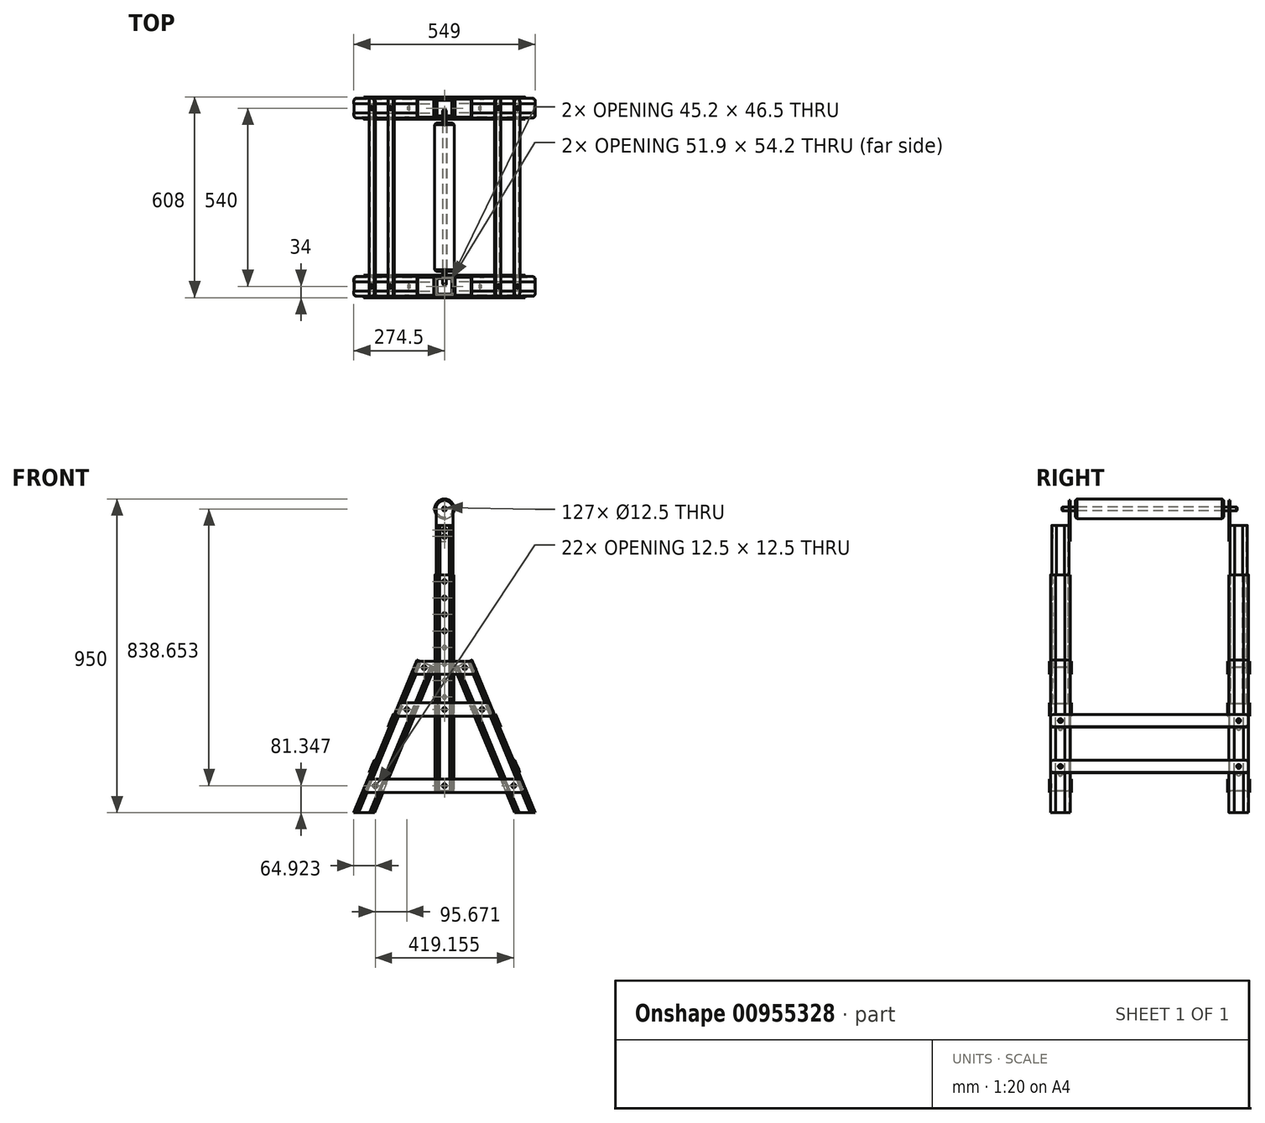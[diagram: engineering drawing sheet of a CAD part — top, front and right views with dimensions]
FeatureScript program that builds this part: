
annotation { "Feature Type Name" : "Feature", "Feature Type Description" : "" }
export const myFeature = defineFeature(function(context is Context, id is Id, definition is map)
    precondition{}
    {
        {
            var Q0;
            Q0=qCreatedBy(makeId("Front.planeOp"),FACE);
            var sketch = newSketch(context, id + "F0", { "sketchPlane" : qUnion([Q0])});
            skLineSegment(sketch, "E0", {"start": v(0, 0) * mm, "end": v(-62.45, 0) * mm});
            skLineSegment(sketch, "E1", {"start": v(-62.45, 0) * mm, "end": v(-244.65, 439.86) * mm});
            skLineSegment(sketch, "E2", {"start": v(-244.65, 439.86) * mm, "end": v(-191.34, 461.94) * mm});
            skLineSegment(sketch, "E3", {"start": v(-191.34, 461.94) * mm, "end": v(0, 0) * mm});
            skLineSegment(sketch, "E4", {"start": v(-218, 450.9) * mm, "end": v(-31.23, 0) * mm, "construction": true});
            skCircle(sketch, "E5", {"center": v(-213.02, 438.89) * mm, "radius": 6.25 * mm});
            skCircle(sketch, "E6", {"center": v(-64.92, 81.35) * mm, "radius": 6.25 * mm});
            skCircle(sketch, "E7", {"center": v(-160.6, 312.32) * mm, "radius": 6.25 * mm});
            skSolve(sketch);
        }
        {
            var Q0;
            Q0 = qSketchRegion(id + "F0", true);
            extrude(context, id + "F1", {"entities" : qUnion([Q0]), "depth" : 60 * mm, "offsetDistance" : 25 * mm});
        }
        {
            var Q0;
            Q0=makeQuery(id+"F1.opExtrude","SWEPT_FACE",FACE,{"disambiguationData":[OSD([sQuery(id+"F0.wireOp",EDGE,"E3")])]});
            var sketch = newSketch(context, id + "F2", { "sketchPlane" : qUnion([Q0])});
            skLineSegment(sketch, "E8", {"start": v(-30, 500) * mm, "end": v(-30, 0) * mm, "construction": true});
            skCircle(sketch, "E9", {"center": v(-30, 150) * mm, "radius": 6.25 * mm});
            skCircle(sketch, "E10", {"center": v(-30, 300) * mm, "radius": 6.25 * mm});
            skSolve(sketch);
        }
        {
            var Q0;
            Q0 = qSketchRegion(id + "F2", true);
            var Q1;
            Q1=makeQuery(id+"F1.opExtrude","SWEPT_FACE",FACE,{"disambiguationData":[OSD([sQuery(id+"F0.wireOp",EDGE,"E1")])]});
            extrude(context, id + "F3", {"entities" : qUnion([Q0]), "operationType" : NewBodyOperationType.REMOVE, "endBound" : BoundingType.UP_TO_SURFACE, "oppositeDirection" : true, "depth" : 25 * mm, "endBoundEntityFace" : qUnion([Q1]), "offsetDistance" : 25 * mm});
        }
        {
            var Q0;
            Q0=makeQuery(id+"F1.opExtrude","CAP_EDGE",EDGE,{"disambiguationData":[OSD([sQuery(id+"F0.wireOp",EDGE,"E1")])],"isStart":false});
            var Q1;
            Q1=makeQuery(id+"F1.opExtrude","CAP_EDGE",EDGE,{"disambiguationData":[OSD([sQuery(id+"F0.wireOp",EDGE,"E3")])],"isStart":false});
            var Q2;
            Q2=makeQuery(id+"F1.opExtrude","CAP_EDGE",EDGE,{"disambiguationData":[OSD([sQuery(id+"F0.wireOp",EDGE,"E1")])],"isStart":true});
            var Q3;
            Q3=makeQuery(id+"F1.opExtrude","CAP_EDGE",EDGE,{"disambiguationData":[OSD([sQuery(id+"F0.wireOp",EDGE,"E3")])],"isStart":true});
            fillet(context, id + "F4", {"entities" : qUnion([Q0, Q1, Q2, Q3]), "radius" : 7.5 * mm, "tangentPropagation" : true, "allowEdgeOverflow" : false});
        }
        {
            var Q0;
            Q0=makeQuery(id+"F1.opExtrude","SWEPT_FACE",FACE,{"disambiguationData":[OSD([sQuery(id+"F0.wireOp",EDGE,"E2")])]});
            var sketch = newSketch(context, id + "F5", { "sketchPlane" : qUnion([Q0])});
            skLineSegment(sketch, "E11", {"start": v(-57.7, -30) * mm, "end": v(-28.85, -30) * mm, "construction": true});
            skLineSegment(sketch, "E12", {"start": v(-28.85, -30) * mm, "end": v(-28.85, -60) * mm, "construction": true});
            skArc(sketch, "E13.0", {"start": v(-54.8, -52.5) * mm, "mid": v(-53.45, -55.75) * mm, "end": v(-50.2, -57.1) * mm});
            skLineSegment(sketch, "E14", {"start": v(-57.4, -30) * mm, "end": v(-57.4, -44) * mm});
            skLineSegment(sketch, "E15", {"start": v(-57.4, -44) * mm, "end": v(-57.7, -44) * mm});
            skLineSegment(sketch, "E16", {"start": v(-50.2, -60) * mm, "end": v(-49.2, -59) * mm});
            skLineSegment(sketch, "E17", {"start": v(-49.2, -59) * mm, "end": v(-48.2, -60) * mm});
            skLineSegment(sketch, "E18", {"start": v(-48.2, -60) * mm, "end": v(-47.2, -59) * mm});
            skLineSegment(sketch, "E19", {"start": v(-47.2, -59) * mm, "end": v(-46.2, -60) * mm});
            skLineSegment(sketch, "E20", {"start": v(-46.2, -60) * mm, "end": v(-45.2, -59) * mm});
            skLineSegment(sketch, "E21", {"start": v(-45.2, -59) * mm, "end": v(-44.2, -60) * mm});
            skLineSegment(sketch, "E22", {"start": v(-50.2, -57.1) * mm, "end": v(-28.85, -57.1) * mm});
            skLineSegment(sketch, "E23", {"start": v(-54.8, -52.5) * mm, "end": v(-54.8, -30) * mm});
            skLineSegment(sketch, "E24.MirrorCS", {"start": v(-0.3, -44) * mm, "end": v(0, -44) * mm});
            skLineSegment(sketch, "E25.MirrorCS", {"start": v(-12.5, -59) * mm, "end": v(-13.5, -60) * mm});
            skLineSegment(sketch, "E26.MirrorCS", {"start": v(-7.5, -60) * mm, "end": v(-8.5, -59) * mm});
            skLineSegment(sketch, "E27.MirrorCS", {"start": v(-8.5, -59) * mm, "end": v(-9.5, -60) * mm});
            skLineSegment(sketch, "E28.MirrorCS", {"start": v(-11.5, -60) * mm, "end": v(-12.5, -59) * mm});
            skLineSegment(sketch, "E29.MirrorCS", {"start": v(-10.5, -59) * mm, "end": v(-11.5, -60) * mm});
            skLineSegment(sketch, "E30.MirrorCS", {"start": v(-9.5, -60) * mm, "end": v(-10.5, -59) * mm});
            skLineSegment(sketch, "E31.MirrorCS", {"start": v(-0.3, -30) * mm, "end": v(-0.3, -44) * mm});
            skLineSegment(sketch, "E32.MirrorCS", {"start": v(-7.5, -57.1) * mm, "end": v(-28.85, -57.1) * mm});
            skLineSegment(sketch, "E33.MirrorCS", {"start": v(-2.9, -52.5) * mm, "end": v(-2.9, -30) * mm});
            skArc(sketch, "E34.MirrorCS", {"start": v(-2.9, -52.5) * mm, "mid": v(-4.25, -55.75) * mm, "end": v(-7.5, -57.1) * mm});
            skLineSegment(sketch, "E35.MirrorCS", {"start": v(-57.4, -16) * mm, "end": v(-57.7, -16) * mm});
            skLineSegment(sketch, "E36.MirrorCS", {"start": v(-50.2, 0) * mm, "end": v(-49.2, -1) * mm});
            skLineSegment(sketch, "E37.MirrorCS", {"start": v(-45.2, -1) * mm, "end": v(-44.2, 0) * mm});
            skLineSegment(sketch, "E38.MirrorCS", {"start": v(-47.2, -1) * mm, "end": v(-46.2, 0) * mm});
            skLineSegment(sketch, "E39.MirrorCS", {"start": v(-48.2, 0) * mm, "end": v(-47.2, -1) * mm});
            skLineSegment(sketch, "E40.MirrorCS", {"start": v(-49.2, -1) * mm, "end": v(-48.2, 0) * mm});
            skLineSegment(sketch, "E41.MirrorCS", {"start": v(-46.2, 0) * mm, "end": v(-45.2, -1) * mm});
            skLineSegment(sketch, "E42.MirrorCS", {"start": v(-57.4, -30) * mm, "end": v(-57.4, -16) * mm});
            skArc(sketch, "E43.MirrorCS", {"start": v(-54.8, -7.5) * mm, "mid": v(-53.45, -4.25) * mm, "end": v(-50.2, -2.9) * mm});
            skLineSegment(sketch, "E44.MirrorCS", {"start": v(-50.2, -2.9) * mm, "end": v(-28.85, -2.9) * mm});
            skLineSegment(sketch, "E45.MirrorCS", {"start": v(-54.8, -7.5) * mm, "end": v(-54.8, -30) * mm});
            skLineSegment(sketch, "E46.MirrorCS", {"start": v(-0.3, -16) * mm, "end": v(0, -16) * mm});
            skLineSegment(sketch, "E47.MirrorCS", {"start": v(-8.5, -1) * mm, "end": v(-9.5, 0) * mm});
            skLineSegment(sketch, "E48.MirrorCS", {"start": v(-11.5, 0) * mm, "end": v(-12.5, -1) * mm});
            skLineSegment(sketch, "E49.MirrorCS", {"start": v(-10.5, -1) * mm, "end": v(-11.5, 0) * mm});
            skLineSegment(sketch, "E50.MirrorCS", {"start": v(-9.5, 0) * mm, "end": v(-10.5, -1) * mm});
            skLineSegment(sketch, "E51.MirrorCS", {"start": v(-12.5, -1) * mm, "end": v(-13.5, 0) * mm});
            skLineSegment(sketch, "E52.MirrorCS", {"start": v(-7.5, 0) * mm, "end": v(-8.5, -1) * mm});
            skLineSegment(sketch, "E53.MirrorCS", {"start": v(-0.3, -30) * mm, "end": v(-0.3, -16) * mm});
            skLineSegment(sketch, "E54.MirrorCS", {"start": v(-2.9, -7.5) * mm, "end": v(-2.9, -30) * mm});
            skArc(sketch, "E55.MirrorCS", {"start": v(-2.9, -7.5) * mm, "mid": v(-4.25, -4.25) * mm, "end": v(-7.5, -2.9) * mm});
            skLineSegment(sketch, "E56.MirrorCS", {"start": v(-7.5, -2.9) * mm, "end": v(-28.85, -2.9) * mm});
            skSolve(sketch);
        }
        {
            var Q0;
            {var subQ0=sQuery(id+"F5.wireOp",EDGE,"E20");Q0=makeQuery(id+"F5.imprint","IMPRINT",FACE,{"disambiguationData":[TD([[makeQuery(id+"F5.imprint","IMPRINT",EDGE,{"derivedFrom":subQ0}),-1.0]])]});}
            var Q1;
            {var subQ0=sQuery(id+"F5.wireOp",EDGE,"E18");Q1=makeQuery(id+"F5.imprint","IMPRINT",FACE,{"disambiguationData":[TD([[makeQuery(id+"F5.imprint","IMPRINT",EDGE,{"derivedFrom":subQ0}),-1.0]])]});}
            var Q2;
            {var subQ0=sQuery(id+"F5.wireOp",EDGE,"E16");Q2=makeQuery(id+"F5.imprint","IMPRINT",FACE,{"disambiguationData":[TD([[makeQuery(id+"F5.imprint","IMPRINT",EDGE,{"derivedFrom":subQ0}),-1.0]])]});}
            var Q3;
            {var subQ0=sQuery(id+"F5.wireOp",EDGE,"E26.MirrorCS");Q3=makeQuery(id+"F5.imprint","IMPRINT",FACE,{"disambiguationData":[TD([[makeQuery(id+"F5.imprint","IMPRINT",EDGE,{"derivedFrom":subQ0}),1.0]])]});}
            var Q4;
            {var subQ0=sQuery(id+"F5.wireOp",EDGE,"E29.MirrorCS");Q4=makeQuery(id+"F5.imprint","IMPRINT",FACE,{"disambiguationData":[TD([[makeQuery(id+"F5.imprint","IMPRINT",EDGE,{"derivedFrom":subQ0}),1.0]])]});}
            var Q5;
            {var subQ0=sQuery(id+"F5.wireOp",EDGE,"E25.MirrorCS");Q5=makeQuery(id+"F5.imprint","IMPRINT",FACE,{"disambiguationData":[TD([[makeQuery(id+"F5.imprint","IMPRINT",EDGE,{"derivedFrom":subQ0}),1.0]])]});}
            var Q6;
            {var subQ1=sQuery(id+"F5.wireOp",EDGE,"E24.MirrorCS");Q6=makeQuery(id+"F5.imprint","IMPRINT",FACE,{"disambiguationData":[TD([[makeQuery(id+"F5.imprint","IMPRINT",EDGE,{"derivedFrom":subQ1}),1.0]])]});}
            var Q7;
            Q7=makeQuery(id+"F5.imprint","IMPRINT",FACE,{"disambiguationData":[TD([[makeQuery(id+"F5.imprint","IMPRINT",EDGE,{"derivedFrom":sQuery(id+"F5.wireOp",EDGE,"E14")}),-1.0]])]});
            var Q8;
            {var subQ0=sQuery(id+"F5.wireOp",EDGE,"E36.MirrorCS");Q8=makeQuery(id+"F5.imprint","IMPRINT",FACE,{"disambiguationData":[TD([[makeQuery(id+"F5.imprint","IMPRINT",EDGE,{"derivedFrom":subQ0}),1.0]])]});}
            var Q9;
            {var subQ0=sQuery(id+"F5.wireOp",EDGE,"E38.MirrorCS");Q9=makeQuery(id+"F5.imprint","IMPRINT",FACE,{"disambiguationData":[TD([[makeQuery(id+"F5.imprint","IMPRINT",EDGE,{"derivedFrom":subQ0}),1.0]])]});}
            var Q10;
            {var subQ0=sQuery(id+"F5.wireOp",EDGE,"E37.MirrorCS");Q10=makeQuery(id+"F5.imprint","IMPRINT",FACE,{"disambiguationData":[TD([[makeQuery(id+"F5.imprint","IMPRINT",EDGE,{"derivedFrom":subQ0}),1.0]])]});}
            var Q11;
            {var subQ0=sQuery(id+"F5.wireOp",EDGE,"E47.MirrorCS");Q11=makeQuery(id+"F5.imprint","IMPRINT",FACE,{"disambiguationData":[TD([[makeQuery(id+"F5.imprint","IMPRINT",EDGE,{"derivedFrom":subQ0}),-1.0]])]});}
            var Q12;
            {var subQ0=sQuery(id+"F5.wireOp",EDGE,"E49.MirrorCS");Q12=makeQuery(id+"F5.imprint","IMPRINT",FACE,{"disambiguationData":[TD([[makeQuery(id+"F5.imprint","IMPRINT",EDGE,{"derivedFrom":subQ0}),-1.0]])]});}
            var Q13;
            {var subQ0=sQuery(id+"F5.wireOp",EDGE,"E48.MirrorCS");Q13=makeQuery(id+"F5.imprint","IMPRINT",FACE,{"disambiguationData":[TD([[makeQuery(id+"F5.imprint","IMPRINT",EDGE,{"derivedFrom":subQ0}),-1.0]])]});}
            var Q14;
            Q14=makeQuery(id+"F5.imprint","IMPRINT",FACE,{"disambiguationData":[TD([[makeQuery(id+"F5.imprint","IMPRINT",EDGE,{"derivedFrom":sQuery(id+"F5.wireOp",EDGE,"E13.0")}),1.0]])]});
            var Q15;
            Q15=makeQuery(id+"F1.opExtrude","SWEPT_FACE",FACE,{"disambiguationData":[OSD([sQuery(id+"F0.wireOp",EDGE,"E0")])]});
            extrude(context, id + "F6", {"entities" : qUnion([Q0, Q1, Q2, Q3, Q4, Q5, Q6, Q7, Q8, Q9, Q10, Q11, Q12, Q13, Q14]), "operationType" : NewBodyOperationType.REMOVE, "endBound" : BoundingType.UP_TO_SURFACE, "oppositeDirection" : true, "depth" : 25 * mm, "endBoundEntityFace" : qUnion([Q15]), "offsetDistance" : 25 * mm});
        }
        {
            var Q0;
            Q0=makeQuery(id+"F1.opExtrude","CAP_FACE",FACE,{"disambiguationData":[OSD([sQuery(id+"F0.wireOp",EDGE,"E0"),sQuery(id+"F0.wireOp",EDGE,"E1"),sQuery(id+"F0.wireOp",EDGE,"E2"),sQuery(id+"F0.wireOp",EDGE,"E3"),sQuery(id+"F0.wireOp",EDGE,"E5"),sQuery(id+"F0.wireOp",EDGE,"E6")])],"isStart":false});
            var sketch = newSketch(context, id + "F7", { "sketchPlane" : qUnion([Q0])});
            skLineSegment(sketch, "E57", {"start": v(-245.65, 720) * mm, "end": v(-245.65, 66.35) * mm});
            skLineSegment(sketch, "E58", {"start": v(-245.65, 66.35) * mm, "end": v(-303.35, 66.35) * mm});
            skLineSegment(sketch, "E59", {"start": v(-303.35, 66.35) * mm, "end": v(-303.35, 720) * mm});
            skLineSegment(sketch, "E60", {"start": v(-303.35, 720) * mm, "end": v(-245.65, 720) * mm});
            skLineSegment(sketch, "E61", {"start": v(-303.35, 75.1) * mm, "end": v(24.53, 75.1) * mm, "construction": true});
            skLineSegment(sketch, "E62", {"start": v(-274.5, 720) * mm, "end": v(-274.5, 66.35) * mm, "construction": true});
            skCircle(sketch, "E63", {"center": v(-274.5, 81.35) * mm, "radius": 6.25 * mm});
            skLineSegment(sketch, "E64", {"start": v(-303.35, 306.07) * mm, "end": v(155.56, 306.07) * mm, "construction": true});
            skCircle(sketch, "E65", {"center": v(-274.5, 312.32) * mm, "radius": 6.25 * mm});
            skCircle(sketch, "E66", {"center": v(-274.5, 650) * mm, "radius": 6.25 * mm});
            skCircle(sketch, "E67", {"center": v(-274.5, 600) * mm, "radius": 6.25 * mm});
            skCircle(sketch, "E68", {"center": v(-274.5, 700) * mm, "radius": 6.25 * mm});
            skCircle(sketch, "E69", {"center": v(-274.5, 550) * mm, "radius": 6.25 * mm});
            skSolve(sketch);
        }
        {
            var Q0;
            Q0 = qSketchRegion(id + "F7", true);
            extrude(context, id + "F8", {"entities" : qUnion([Q0]), "oppositeDirection" : true, "depth" : 60 * mm, "offsetDistance" : 25 * mm});
        }
        {
            var Q0;
            Q0=makeQuery(id+"F8.opExtrude","CAP_EDGE",EDGE,{"disambiguationData":[OSD([sQuery(id+"F7.wireOp",EDGE,"E59")])],"isStart":false});
            var Q1;
            Q1=makeQuery(id+"F8.opExtrude","CAP_EDGE",EDGE,{"disambiguationData":[OSD([sQuery(id+"F7.wireOp",EDGE,"E59")])],"isStart":true});
            var Q2;
            Q2=makeQuery(id+"F8.opExtrude","CAP_EDGE",EDGE,{"disambiguationData":[OSD([sQuery(id+"F7.wireOp",EDGE,"E57")])],"isStart":true});
            var Q3;
            Q3=makeQuery(id+"F8.opExtrude","CAP_EDGE",EDGE,{"disambiguationData":[OSD([sQuery(id+"F7.wireOp",EDGE,"E57")])],"isStart":false});
            fillet(context, id + "F9", {"entities" : qUnion([Q0, Q1, Q2, Q3]), "radius" : 7.5 * mm, "tangentPropagation" : true, "allowEdgeOverflow" : false});
        }
        {
            var Q0;
            Q0=makeQuery(id+"F8.opExtrude","SWEPT_FACE",FACE,{"disambiguationData":[OSD([sQuery(id+"F7.wireOp",EDGE,"E60")])]});
            var sketch = newSketch(context, id + "F10", { "sketchPlane" : qUnion([Q0])});
            skLineSegment(sketch, "E70", {"start": v(-274.5, -60) * mm, "end": v(-274.5, -30) * mm, "construction": true});
            skPoint(sketch, "E70.endSnap0", {"position": v(-303.35, -30) * mm});
            skLineSegment(sketch, "E71", {"start": v(-274.5, -30) * mm, "end": v(-303.35, -30) * mm, "construction": true});
            skLineSegment(sketch, "E72", {"start": v(-295.85, -60) * mm, "end": v(-294.85, -59) * mm});
            skLineSegment(sketch, "E73", {"start": v(-294.85, -59) * mm, "end": v(-293.85, -60) * mm});
            skLineSegment(sketch, "E74", {"start": v(-293.85, -60) * mm, "end": v(-292.85, -59) * mm});
            skLineSegment(sketch, "E75", {"start": v(-292.85, -59) * mm, "end": v(-291.85, -60) * mm});
            skLineSegment(sketch, "E76", {"start": v(-291.85, -60) * mm, "end": v(-290.85, -59) * mm});
            skLineSegment(sketch, "E77", {"start": v(-290.85, -59) * mm, "end": v(-289.85, -60) * mm});
            skLineSegment(sketch, "E78", {"start": v(-303.05, -30) * mm, "end": v(-303.05, -44) * mm});
            skLineSegment(sketch, "E79", {"start": v(-303.05, -44) * mm, "end": v(-303.35, -44) * mm});
            skArc(sketch, "E80.0", {"start": v(-300.45, -52.5) * mm, "mid": v(-299.1, -55.75) * mm, "end": v(-295.85, -57.1) * mm});
            skLineSegment(sketch, "E81", {"start": v(-295.85, -57.1) * mm, "end": v(-274.5, -57.1) * mm});
            skLineSegment(sketch, "E82", {"start": v(-300.45, -52.5) * mm, "end": v(-300.45, -30) * mm});
            skLineSegment(sketch, "E83.MirrorCS", {"start": v(-255.15, -60) * mm, "end": v(-256.15, -59) * mm});
            skLineSegment(sketch, "E84.MirrorCS", {"start": v(-245.95, -44) * mm, "end": v(-245.65, -44) * mm});
            skLineSegment(sketch, "E85.MirrorCS", {"start": v(-254.15, -59) * mm, "end": v(-255.15, -60) * mm});
            skLineSegment(sketch, "E86.MirrorCS", {"start": v(-256.15, -59) * mm, "end": v(-257.15, -60) * mm});
            skLineSegment(sketch, "E87.MirrorCS", {"start": v(-257.15, -60) * mm, "end": v(-258.15, -59) * mm});
            skLineSegment(sketch, "E88.MirrorCS", {"start": v(-253.15, -60) * mm, "end": v(-254.15, -59) * mm});
            skLineSegment(sketch, "E89.MirrorCS", {"start": v(-258.15, -59) * mm, "end": v(-259.15, -60) * mm});
            skLineSegment(sketch, "E90.MirrorCS", {"start": v(-248.55, -52.5) * mm, "end": v(-248.55, -30) * mm});
            skLineSegment(sketch, "E91.MirrorCS", {"start": v(-245.95, -30) * mm, "end": v(-245.95, -44) * mm});
            skLineSegment(sketch, "E92.MirrorCS", {"start": v(-253.15, -57.1) * mm, "end": v(-274.5, -57.1) * mm});
            skArc(sketch, "E93.MirrorCS", {"start": v(-248.55, -52.5) * mm, "mid": v(-249.9, -55.75) * mm, "end": v(-253.15, -57.1) * mm});
            skLineSegment(sketch, "E94.MirrorCS", {"start": v(-290.85, -1) * mm, "end": v(-289.85, 0) * mm});
            skLineSegment(sketch, "E95.MirrorCS", {"start": v(-303.05, -16) * mm, "end": v(-303.35, -16) * mm});
            skLineSegment(sketch, "E96.MirrorCS", {"start": v(-295.85, 0) * mm, "end": v(-294.85, -1) * mm});
            skLineSegment(sketch, "E97.MirrorCS", {"start": v(-293.85, 0) * mm, "end": v(-292.85, -1) * mm});
            skLineSegment(sketch, "E98.MirrorCS", {"start": v(-294.85, -1) * mm, "end": v(-293.85, 0) * mm});
            skLineSegment(sketch, "E99.MirrorCS", {"start": v(-291.85, 0) * mm, "end": v(-290.85, -1) * mm});
            skLineSegment(sketch, "E100.MirrorCS", {"start": v(-292.85, -1) * mm, "end": v(-291.85, 0) * mm});
            skLineSegment(sketch, "E101.MirrorCS", {"start": v(-300.45, -7.5) * mm, "end": v(-300.45, -30) * mm});
            skLineSegment(sketch, "E102.MirrorCS", {"start": v(-295.85, -2.9) * mm, "end": v(-274.5, -2.9) * mm});
            skArc(sketch, "E103.MirrorCS", {"start": v(-300.45, -7.5) * mm, "mid": v(-299.1, -4.25) * mm, "end": v(-295.85, -2.9) * mm});
            skLineSegment(sketch, "E104.MirrorCS", {"start": v(-303.05, -30) * mm, "end": v(-303.05, -16) * mm});
            skLineSegment(sketch, "E105.MirrorCS", {"start": v(-253.15, 0) * mm, "end": v(-254.15, -1) * mm});
            skLineSegment(sketch, "E106.MirrorCS", {"start": v(-258.15, -1) * mm, "end": v(-259.15, 0) * mm});
            skLineSegment(sketch, "E107.MirrorCS", {"start": v(-255.15, 0) * mm, "end": v(-256.15, -1) * mm});
            skLineSegment(sketch, "E108.MirrorCS", {"start": v(-257.15, 0) * mm, "end": v(-258.15, -1) * mm});
            skLineSegment(sketch, "E109.MirrorCS", {"start": v(-256.15, -1) * mm, "end": v(-257.15, 0) * mm});
            skLineSegment(sketch, "E110.MirrorCS", {"start": v(-245.95, -16) * mm, "end": v(-245.65, -16) * mm});
            skLineSegment(sketch, "E111.MirrorCS", {"start": v(-254.15, -1) * mm, "end": v(-255.15, 0) * mm});
            skLineSegment(sketch, "E112.MirrorCS", {"start": v(-248.55, -7.5) * mm, "end": v(-248.55, -30) * mm});
            skLineSegment(sketch, "E113.MirrorCS", {"start": v(-245.95, -30) * mm, "end": v(-245.95, -16) * mm});
            skArc(sketch, "E114.MirrorCS", {"start": v(-248.55, -7.5) * mm, "mid": v(-249.9, -4.25) * mm, "end": v(-253.15, -2.9) * mm});
            skLineSegment(sketch, "E115.MirrorCS", {"start": v(-253.15, -2.9) * mm, "end": v(-274.5, -2.9) * mm});
            skSolve(sketch);
        }
        {
            var Q0;
            {var subQ0=sQuery(id+"F10.wireOp",EDGE,"E76");Q0=makeQuery(id+"F10.imprint","IMPRINT",FACE,{"disambiguationData":[TD([[makeQuery(id+"F10.imprint","IMPRINT",EDGE,{"derivedFrom":subQ0}),-1.0]])]});}
            var Q1;
            {var subQ0=sQuery(id+"F10.wireOp",EDGE,"E74");Q1=makeQuery(id+"F10.imprint","IMPRINT",FACE,{"disambiguationData":[TD([[makeQuery(id+"F10.imprint","IMPRINT",EDGE,{"derivedFrom":subQ0}),-1.0]])]});}
            var Q2;
            {var subQ0=sQuery(id+"F10.wireOp",EDGE,"E72");Q2=makeQuery(id+"F10.imprint","IMPRINT",FACE,{"disambiguationData":[TD([[makeQuery(id+"F10.imprint","IMPRINT",EDGE,{"derivedFrom":subQ0}),-1.0]])]});}
            var Q3;
            Q3=makeQuery(id+"F10.imprint","IMPRINT",FACE,{"disambiguationData":[TD([[makeQuery(id+"F10.imprint","IMPRINT",EDGE,{"derivedFrom":sQuery(id+"F10.wireOp",EDGE,"E78")}),-1.0]])]});
            var Q4;
            {var subQ0=sQuery(id+"F10.wireOp",EDGE,"E85.MirrorCS");Q4=makeQuery(id+"F10.imprint","IMPRINT",FACE,{"disambiguationData":[TD([[makeQuery(id+"F10.imprint","IMPRINT",EDGE,{"derivedFrom":subQ0}),1.0]])]});}
            var Q5;
            {var subQ0=sQuery(id+"F10.wireOp",EDGE,"E83.MirrorCS");Q5=makeQuery(id+"F10.imprint","IMPRINT",FACE,{"disambiguationData":[TD([[makeQuery(id+"F10.imprint","IMPRINT",EDGE,{"derivedFrom":subQ0}),1.0]])]});}
            var Q6;
            {var subQ0=sQuery(id+"F10.wireOp",EDGE,"E87.MirrorCS");Q6=makeQuery(id+"F10.imprint","IMPRINT",FACE,{"disambiguationData":[TD([[makeQuery(id+"F10.imprint","IMPRINT",EDGE,{"derivedFrom":subQ0}),1.0]])]});}
            var Q7;
            {var subQ1=sQuery(id+"F10.wireOp",EDGE,"E84.MirrorCS");Q7=makeQuery(id+"F10.imprint","IMPRINT",FACE,{"disambiguationData":[TD([[makeQuery(id+"F10.imprint","IMPRINT",EDGE,{"derivedFrom":subQ1}),1.0]])]});}
            var Q8;
            {var subQ0=sQuery(id+"F10.wireOp",EDGE,"E105.MirrorCS");Q8=makeQuery(id+"F10.imprint","IMPRINT",FACE,{"disambiguationData":[TD([[makeQuery(id+"F10.imprint","IMPRINT",EDGE,{"derivedFrom":subQ0}),-1.0]])]});}
            var Q9;
            {var subQ0=sQuery(id+"F10.wireOp",EDGE,"E107.MirrorCS");Q9=makeQuery(id+"F10.imprint","IMPRINT",FACE,{"disambiguationData":[TD([[makeQuery(id+"F10.imprint","IMPRINT",EDGE,{"derivedFrom":subQ0}),-1.0]])]});}
            var Q10;
            {var subQ0=sQuery(id+"F10.wireOp",EDGE,"E106.MirrorCS");Q10=makeQuery(id+"F10.imprint","IMPRINT",FACE,{"disambiguationData":[TD([[makeQuery(id+"F10.imprint","IMPRINT",EDGE,{"derivedFrom":subQ0}),-1.0]])]});}
            var Q11;
            {var subQ0=sQuery(id+"F10.wireOp",EDGE,"E96.MirrorCS");Q11=makeQuery(id+"F10.imprint","IMPRINT",FACE,{"disambiguationData":[TD([[makeQuery(id+"F10.imprint","IMPRINT",EDGE,{"derivedFrom":subQ0}),1.0]])]});}
            var Q12;
            {var subQ0=sQuery(id+"F10.wireOp",EDGE,"E97.MirrorCS");Q12=makeQuery(id+"F10.imprint","IMPRINT",FACE,{"disambiguationData":[TD([[makeQuery(id+"F10.imprint","IMPRINT",EDGE,{"derivedFrom":subQ0}),1.0]])]});}
            var Q13;
            {var subQ0=sQuery(id+"F10.wireOp",EDGE,"E94.MirrorCS");Q13=makeQuery(id+"F10.imprint","IMPRINT",FACE,{"disambiguationData":[TD([[makeQuery(id+"F10.imprint","IMPRINT",EDGE,{"derivedFrom":subQ0}),1.0]])]});}
            var Q14;
            Q14=makeQuery(id+"F10.imprint","IMPRINT",FACE,{"disambiguationData":[TD([[makeQuery(id+"F10.imprint","IMPRINT",EDGE,{"derivedFrom":sQuery(id+"F10.wireOp",EDGE,"E80.0")}),1.0]])]});
            var Q15;
            Q15=makeQuery(id+"F8.opExtrude","SWEPT_FACE",FACE,{"disambiguationData":[OSD([sQuery(id+"F7.wireOp",EDGE,"E58")])]});
            extrude(context, id + "F11", {"entities" : qUnion([Q0, Q1, Q2, Q3, Q4, Q5, Q6, Q7, Q8, Q9, Q10, Q11, Q12, Q13, Q14]), "operationType" : NewBodyOperationType.REMOVE, "endBound" : BoundingType.UP_TO_SURFACE, "oppositeDirection" : true, "depth" : 25 * mm, "endBoundEntityFace" : qUnion([Q15]), "offsetDistance" : 25 * mm});
        }
        {
            var Q0;
            Q0=makeQuery(id+"F11.boolean.opBoolean","COPY",FACE,{"derivedFrom":makeQuery(id+"F11.opExtrude","SWEPT_FACE",FACE,{"disambiguationData":[OSD([sQuery(id+"F10.wireOp",EDGE,"E82"),sQuery(id+"F10.wireOp",EDGE,"E101.MirrorCS")])]})});
            var Q1;
            Q1=makeQuery(id+"F11.boolean.opBoolean","COPY",FACE,{"derivedFrom":makeQuery(id+"F11.opExtrude","SWEPT_FACE",FACE,{"disambiguationData":[OSD([sQuery(id+"F10.wireOp",EDGE,"E90.MirrorCS"),sQuery(id+"F10.wireOp",EDGE,"E112.MirrorCS")])]})});
            cPlane(context, id + "F12", {"entities" : qUnion([Q0, Q1]), "cplaneType" : CPlaneType.MID_PLANE, "offset" : 25 * mm, "width" : 150 * mm, "height" : 150 * mm});
        }
        {
            var Q0;
            Q0=makeQuery(id+"F11.boolean.opBoolean","COPY",FACE,{"derivedFrom":makeQuery(id+"F11.opExtrude","SWEPT_FACE",FACE,{"disambiguationData":[OSD([sQuery(id+"F10.wireOp",EDGE,"E81"),sQuery(id+"F10.wireOp",EDGE,"E92.MirrorCS")])]})});
            var Q1;
            Q1=makeQuery(id+"F11.boolean.opBoolean","COPY",FACE,{"derivedFrom":makeQuery(id+"F11.opExtrude","SWEPT_FACE",FACE,{"disambiguationData":[OSD([sQuery(id+"F10.wireOp",EDGE,"E102.MirrorCS"),sQuery(id+"F10.wireOp",EDGE,"E115.MirrorCS")])]})});
            cPlane(context, id + "F13", {"entities" : qUnion([Q0, Q1]), "cplaneType" : CPlaneType.MID_PLANE, "offset" : 25 * mm, "width" : 150 * mm, "height" : 150 * mm});
        }
        {
            var Q0;
            Q0=makeQuery(id+"F8.opExtrude","CAP_EDGE",EDGE,{"disambiguationData":[OSD([sQuery(id+"F7.wireOp",EDGE,"E65")])],"isStart":false});
            cPlane(context, id + "F14", {"entities" : qUnion([Q0]), "cplaneType" : CPlaneType.LINE_ANGLE, "offset" : 25 * mm, "angle" : 0 * degree, "width" : 150 * mm, "height" : 150 * mm});
        }
        {
            var Q0;
            Q0=qCreatedBy(id+"F13.planeOp",FACE);
            var sketch = newSketch(context, id + "F15", { "sketchPlane" : qUnion([Q0])});
            skLineSegment(sketch, "E116", {"start": v(249, 870) * mm, "end": v(249, 330) * mm});
            skLineSegment(sketch, "E117", {"start": v(249, 330) * mm, "end": v(300, 330) * mm});
            skLineSegment(sketch, "E118", {"start": v(300, 330) * mm, "end": v(300, 870) * mm});
            skLineSegment(sketch, "E119", {"start": v(300, 870) * mm, "end": v(249, 870) * mm});
            skLineSegment(sketch, "E120", {"start": v(274.5, 870) * mm, "end": v(274.5, 330) * mm, "construction": true});
            skCircle(sketch, "E121", {"center": v(274.5, 550) * mm, "radius": 6.25 * mm});
            skCircle(sketch, "E122", {"center": v(274.5, 500) * mm, "radius": 6.25 * mm});
            skCircle(sketch, "E123", {"center": v(274.5, 650) * mm, "radius": 6.25 * mm});
            skCircle(sketch, "E124", {"center": v(274.5, 450) * mm, "radius": 6.25 * mm});
            skCircle(sketch, "E125", {"center": v(274.5, 700) * mm, "radius": 6.25 * mm});
            skCircle(sketch, "E126", {"center": v(274.5, 600) * mm, "radius": 6.25 * mm});
            skCircle(sketch, "E127", {"center": v(274.5, 400) * mm, "radius": 6.25 * mm});
            skCircle(sketch, "E128", {"center": v(274.5, 350) * mm, "radius": 6.25 * mm});
            skCircle(sketch, "E129", {"center": v(274.5, 856.25) * mm, "radius": 6.25 * mm});
            skCircle(sketch, "E130", {"center": v(274.5, 836.25) * mm, "radius": 6.25 * mm});
            skSolve(sketch);
        }
        {
            var Q0;
            Q0 = qSketchRegion(id + "F15", true);
            extrude(context, id + "F16", {"entities" : qUnion([Q0]), "endBound" : BoundingType.SYMMETRIC, "depth" : 52.3 * mm, "offsetDistance" : 25 * mm});
        }
        {
            var Q0;
            Q0=makeQuery(id+"F16.opExtrude","CAP_EDGE",EDGE,{"disambiguationData":[OSD([sQuery(id+"F15.wireOp",EDGE,"E116")])],"isStart":true});
            var Q1;
            Q1=makeQuery(id+"F16.opExtrude","CAP_EDGE",EDGE,{"disambiguationData":[OSD([sQuery(id+"F15.wireOp",EDGE,"E118")])],"isStart":true});
            var Q2;
            Q2=makeQuery(id+"F16.opExtrude","CAP_EDGE",EDGE,{"disambiguationData":[OSD([sQuery(id+"F15.wireOp",EDGE,"E116")])],"isStart":false});
            var Q3;
            Q3=makeQuery(id+"F16.opExtrude","CAP_EDGE",EDGE,{"disambiguationData":[OSD([sQuery(id+"F15.wireOp",EDGE,"E118")])],"isStart":false});
            fillet(context, id + "F17", {"entities" : qUnion([Q0, Q1, Q2, Q3]), "radius" : 7.5 * mm, "tangentPropagation" : true, "allowEdgeOverflow" : false});
        }
        {
            var Q0;
            Q0=makeQuery(id+"F16.opExtrude","SWEPT_FACE",FACE,{"disambiguationData":[OSD([sQuery(id+"F15.wireOp",EDGE,"E119")])]});
            var sketch = newSketch(context, id + "F18", { "sketchPlane" : qUnion([Q0])});
            skLineSegment(sketch, "E131", {"start": v(-249, -30) * mm, "end": v(-274.5, -30) * mm, "construction": true});
            skPoint(sketch, "E131.endSnap0", {"position": v(-274.5, -3.85) * mm});
            skLineSegment(sketch, "E132", {"start": v(-274.5, -30) * mm, "end": v(-274.5, -3.85) * mm, "construction": true});
            skLineSegment(sketch, "E133", {"start": v(-256.5, -3.85) * mm, "end": v(-257.5, -4.85) * mm});
            skLineSegment(sketch, "E134", {"start": v(-257.5, -4.85) * mm, "end": v(-258.5, -3.85) * mm});
            skLineSegment(sketch, "E135", {"start": v(-258.5, -3.85) * mm, "end": v(-259.5, -4.85) * mm});
            skLineSegment(sketch, "E136", {"start": v(-259.5, -4.85) * mm, "end": v(-260.5, -3.85) * mm});
            skLineSegment(sketch, "E137", {"start": v(-249.25, -30) * mm, "end": v(-249.25, -17.85) * mm});
            skLineSegment(sketch, "E138", {"start": v(-249.25, -17.85) * mm, "end": v(-249, -17.85) * mm});
            skArc(sketch, "E139.0", {"start": v(-251.9, -11.35) * mm, "mid": v(-253.25, -8.1) * mm, "end": v(-256.5, -6.75) * mm});
            skLineSegment(sketch, "E140", {"start": v(-256.5, -6.75) * mm, "end": v(-274.5, -6.75) * mm});
            skLineSegment(sketch, "E141", {"start": v(-251.9, -11.35) * mm, "end": v(-251.9, -30) * mm});
            skLineSegment(sketch, "E142.MirrorCS", {"start": v(-299.75, -17.85) * mm, "end": v(-300, -17.85) * mm});
            skLineSegment(sketch, "E143.MirrorCS", {"start": v(-292.5, -3.85) * mm, "end": v(-291.5, -4.85) * mm});
            skLineSegment(sketch, "E144.MirrorCS", {"start": v(-290.5, -3.85) * mm, "end": v(-289.5, -4.85) * mm});
            skLineSegment(sketch, "E145.MirrorCS", {"start": v(-289.5, -4.85) * mm, "end": v(-288.5, -3.85) * mm});
            skLineSegment(sketch, "E146.MirrorCS", {"start": v(-291.5, -4.85) * mm, "end": v(-290.5, -3.85) * mm});
            skLineSegment(sketch, "E147.MirrorCS", {"start": v(-299.75, -30) * mm, "end": v(-299.75, -17.85) * mm});
            skLineSegment(sketch, "E148.MirrorCS", {"start": v(-297.1, -11.35) * mm, "end": v(-297.1, -30) * mm});
            skLineSegment(sketch, "E149.MirrorCS", {"start": v(-292.5, -6.75) * mm, "end": v(-274.5, -6.75) * mm});
            skArc(sketch, "E150.MirrorCS", {"start": v(-297.1, -11.35) * mm, "mid": v(-295.75, -8.1) * mm, "end": v(-292.5, -6.75) * mm});
            skLineSegment(sketch, "E151.MirrorCS", {"start": v(-258.5, -56.15) * mm, "end": v(-259.5, -55.15) * mm});
            skLineSegment(sketch, "E152.MirrorCS", {"start": v(-249.25, -42.15) * mm, "end": v(-249, -42.15) * mm});
            skLineSegment(sketch, "E153.MirrorCS", {"start": v(-257.5, -55.15) * mm, "end": v(-258.5, -56.15) * mm});
            skLineSegment(sketch, "E154.MirrorCS", {"start": v(-256.5, -56.15) * mm, "end": v(-257.5, -55.15) * mm});
            skLineSegment(sketch, "E155.MirrorCS", {"start": v(-259.5, -55.15) * mm, "end": v(-260.5, -56.15) * mm});
            skLineSegment(sketch, "E156.MirrorCS", {"start": v(-256.5, -53.25) * mm, "end": v(-274.5, -53.25) * mm});
            skArc(sketch, "E157.MirrorCS", {"start": v(-251.9, -48.65) * mm, "mid": v(-253.25, -51.9) * mm, "end": v(-256.5, -53.25) * mm});
            skLineSegment(sketch, "E158.MirrorCS", {"start": v(-249.25, -30) * mm, "end": v(-249.25, -42.15) * mm});
            skLineSegment(sketch, "E159.MirrorCS", {"start": v(-251.9, -48.65) * mm, "end": v(-251.9, -30) * mm});
            skLineSegment(sketch, "E160.MirrorCS", {"start": v(-299.75, -42.15) * mm, "end": v(-300, -42.15) * mm});
            skLineSegment(sketch, "E161.MirrorCS", {"start": v(-291.5, -55.15) * mm, "end": v(-290.5, -56.15) * mm});
            skLineSegment(sketch, "E162.MirrorCS", {"start": v(-290.5, -56.15) * mm, "end": v(-289.5, -55.15) * mm});
            skLineSegment(sketch, "E163.MirrorCS", {"start": v(-292.5, -56.15) * mm, "end": v(-291.5, -55.15) * mm});
            skLineSegment(sketch, "E164.MirrorCS", {"start": v(-289.5, -55.15) * mm, "end": v(-288.5, -56.15) * mm});
            skLineSegment(sketch, "E165.MirrorCS", {"start": v(-299.75, -30) * mm, "end": v(-299.75, -42.15) * mm});
            skArc(sketch, "E166.MirrorCS", {"start": v(-297.1, -48.65) * mm, "mid": v(-295.75, -51.9) * mm, "end": v(-292.5, -53.25) * mm});
            skLineSegment(sketch, "E167.MirrorCS", {"start": v(-297.1, -48.65) * mm, "end": v(-297.1, -30) * mm});
            skLineSegment(sketch, "E168.MirrorCS", {"start": v(-292.5, -53.25) * mm, "end": v(-274.5, -53.25) * mm});
            skSolve(sketch);
        }
        {
            var Q0;
            Q0=makeQuery(id+"F18.imprint","IMPRINT",FACE,{"disambiguationData":[TD([[makeQuery(id+"F18.imprint","IMPRINT",EDGE,{"derivedFrom":sQuery(id+"F18.wireOp",EDGE,"E137")}),-1.0]])]});
            var Q1;
            {var subQ1=sQuery(id+"F18.wireOp",EDGE,"E142.MirrorCS");Q1=makeQuery(id+"F18.imprint","IMPRINT",FACE,{"disambiguationData":[TD([[makeQuery(id+"F18.imprint","IMPRINT",EDGE,{"derivedFrom":subQ1}),1.0]])]});}
            var Q2;
            {var subQ0=sQuery(id+"F18.wireOp",EDGE,"E161.MirrorCS");Q2=makeQuery(id+"F18.imprint","IMPRINT",FACE,{"disambiguationData":[TD([[makeQuery(id+"F18.imprint","IMPRINT",EDGE,{"derivedFrom":subQ0}),-1.0]])]});}
            var Q3;
            {var subQ0=sQuery(id+"F18.wireOp",EDGE,"E162.MirrorCS");Q3=makeQuery(id+"F18.imprint","IMPRINT",FACE,{"disambiguationData":[TD([[makeQuery(id+"F18.imprint","IMPRINT",EDGE,{"derivedFrom":subQ0}),-1.0]])]});}
            var Q4;
            {var subQ0=sQuery(id+"F18.wireOp",EDGE,"E153.MirrorCS");Q4=makeQuery(id+"F18.imprint","IMPRINT",FACE,{"disambiguationData":[TD([[makeQuery(id+"F18.imprint","IMPRINT",EDGE,{"derivedFrom":subQ0}),1.0]])]});}
            var Q5;
            {var subQ0=sQuery(id+"F18.wireOp",EDGE,"E151.MirrorCS");Q5=makeQuery(id+"F18.imprint","IMPRINT",FACE,{"disambiguationData":[TD([[makeQuery(id+"F18.imprint","IMPRINT",EDGE,{"derivedFrom":subQ0}),1.0]])]});}
            var Q6;
            {var subQ0=sQuery(id+"F18.wireOp",EDGE,"E133");Q6=makeQuery(id+"F18.imprint","IMPRINT",FACE,{"disambiguationData":[TD([[makeQuery(id+"F18.imprint","IMPRINT",EDGE,{"derivedFrom":subQ0}),-1.0]])]});}
            var Q7;
            {var subQ0=sQuery(id+"F18.wireOp",EDGE,"E135");Q7=makeQuery(id+"F18.imprint","IMPRINT",FACE,{"disambiguationData":[TD([[makeQuery(id+"F18.imprint","IMPRINT",EDGE,{"derivedFrom":subQ0}),-1.0]])]});}
            var Q8;
            {var subQ0=sQuery(id+"F18.wireOp",EDGE,"E143.MirrorCS");Q8=makeQuery(id+"F18.imprint","IMPRINT",FACE,{"disambiguationData":[TD([[makeQuery(id+"F18.imprint","IMPRINT",EDGE,{"derivedFrom":subQ0}),1.0]])]});}
            var Q9;
            {var subQ0=sQuery(id+"F18.wireOp",EDGE,"E144.MirrorCS");Q9=makeQuery(id+"F18.imprint","IMPRINT",FACE,{"disambiguationData":[TD([[makeQuery(id+"F18.imprint","IMPRINT",EDGE,{"derivedFrom":subQ0}),1.0]])]});}
            var Q10;
            Q10=makeQuery(id+"F18.imprint","IMPRINT",FACE,{"disambiguationData":[TD([[makeQuery(id+"F18.imprint","IMPRINT",EDGE,{"derivedFrom":sQuery(id+"F18.wireOp",EDGE,"E139.0")}),1.0]])]});
            var Q11;
            Q11=makeQuery(id+"F16.opExtrude","SWEPT_FACE",FACE,{"disambiguationData":[OSD([sQuery(id+"F15.wireOp",EDGE,"E117")])]});
            extrude(context, id + "F19", {"entities" : qUnion([Q0, Q1, Q2, Q3, Q4, Q5, Q6, Q7, Q8, Q9, Q10]), "operationType" : NewBodyOperationType.REMOVE, "endBound" : BoundingType.UP_TO_SURFACE, "oppositeDirection" : true, "depth" : 25 * mm, "endBoundEntityFace" : qUnion([Q11]), "offsetDistance" : 25 * mm});
        }
        {
            var Q0;
            Q0=makeQuery(id+"F1.opExtrude","SWEPT_BODY",BODY,{"disambiguationData":[OSD([sQuery(id+"F0.wireOp",EDGE,"E0"),sQuery(id+"F0.wireOp",EDGE,"E1"),sQuery(id+"F0.wireOp",EDGE,"E2"),sQuery(id+"F0.wireOp",EDGE,"E3"),sQuery(id+"F0.wireOp",EDGE,"E5"),sQuery(id+"F0.wireOp",EDGE,"E6"),sQuery(id+"F0.wireOp",EDGE,"E7")])]});
            var Q1;
            Q1=qCreatedBy(id+"F12.planeOp",FACE);
            mirror(context, id + "F20", {"entities" : qUnion([Q0]), "mirrorPlane" : qUnion([Q1])});
        }
        {
            var Q0;
            Q0=makeQuery(id+"F1.opExtrude","CAP_FACE",FACE,{"disambiguationData":[OSD([sQuery(id+"F0.wireOp",EDGE,"E0"),sQuery(id+"F0.wireOp",EDGE,"E1"),sQuery(id+"F0.wireOp",EDGE,"E2"),sQuery(id+"F0.wireOp",EDGE,"E3"),sQuery(id+"F0.wireOp",EDGE,"E5"),sQuery(id+"F0.wireOp",EDGE,"E6"),sQuery(id+"F0.wireOp",EDGE,"E7")])],"isStart":false});
            var sketch = newSketch(context, id + "F21", { "sketchPlane" : qUnion([Q0])});
            skLineSegment(sketch, "E169", {"start": v(-411.35, 332.32) * mm, "end": v(-427.92, 292.32) * mm});
            skLineSegment(sketch, "E170", {"start": v(-427.92, 292.32) * mm, "end": v(-121.08, 292.32) * mm});
            skLineSegment(sketch, "E171", {"start": v(-121.08, 292.32) * mm, "end": v(-137.65, 332.32) * mm});
            skLineSegment(sketch, "E172", {"start": v(-137.65, 332.32) * mm, "end": v(-411.35, 332.32) * mm});
            skLineSegment(sketch, "E173", {"start": v(-507.02, 101.35) * mm, "end": v(-523.59, 61.35) * mm});
            skLineSegment(sketch, "E174", {"start": v(-523.59, 61.35) * mm, "end": v(-25.41, 61.35) * mm});
            skLineSegment(sketch, "E175", {"start": v(-25.41, 61.35) * mm, "end": v(-41.98, 101.35) * mm});
            skLineSegment(sketch, "E176", {"start": v(-41.98, 101.35) * mm, "end": v(-507.02, 101.35) * mm});
            skLineSegment(sketch, "E177", {"start": v(-419.63, 312.32) * mm, "end": v(-129.37, 312.32) * mm, "construction": true});
            skCircle(sketch, "E178", {"center": v(-388.4, 312.32) * mm, "radius": 6.25 * mm});
            skCircle(sketch, "E179", {"center": v(-274.5, 312.32) * mm, "radius": 6.25 * mm});
            skCircle(sketch, "E180", {"center": v(-160.6, 312.32) * mm, "radius": 6.25 * mm});
            skLineSegment(sketch, "E181", {"start": v(-515.3, 81.35) * mm, "end": v(-33.7, 81.35) * mm, "construction": true});
            skCircle(sketch, "E182", {"center": v(-484.08, 81.35) * mm, "radius": 6.25 * mm});
            skCircle(sketch, "E183", {"center": v(-274.5, 81.35) * mm, "radius": 6.25 * mm});
            skCircle(sketch, "E184", {"center": v(-64.92, 81.35) * mm, "radius": 6.25 * mm});
            skLineSegment(sketch, "E185", {"start": v(-358.92, 458.89) * mm, "end": v(-375.49, 418.89) * mm});
            skLineSegment(sketch, "E186", {"start": v(-375.49, 418.89) * mm, "end": v(-173.5, 418.89) * mm});
            skLineSegment(sketch, "E187", {"start": v(-173.5, 418.89) * mm, "end": v(-190.08, 458.89) * mm});
            skLineSegment(sketch, "E188", {"start": v(-190.08, 458.89) * mm, "end": v(-358.92, 458.89) * mm});
            skLineSegment(sketch, "E189", {"start": v(-367.2, 438.89) * mm, "end": v(-181.8, 438.89) * mm, "construction": true});
            skCircle(sketch, "E190", {"center": v(-213.02, 438.89) * mm, "radius": 6.25 * mm});
            skCircle(sketch, "E191", {"center": v(-335.98, 438.89) * mm, "radius": 6.25 * mm});
            skSolve(sketch);
        }
        {
            var Q0;
            Q0 = qSketchRegion(id + "F21", true);
            extrude(context, id + "F22", {"entities" : qUnion([Q0]), "depth" : 4 * mm, "offsetDistance" : 25 * mm});
        }
        {
            var Q0;
            Q0=makeQuery(id+"F22.opExtrude","SWEPT_EDGE",EDGE,{"disambiguationData":[OSD([sQuery(id+"F21.wireOp",EDGE,"E173"),sQuery(id+"F21.wireOp",EDGE,"E174")])]});
            var Q1;
            Q1=makeQuery(id+"F22.opExtrude","SWEPT_EDGE",EDGE,{"disambiguationData":[OSD([sQuery(id+"F21.wireOp",EDGE,"E173"),sQuery(id+"F21.wireOp",EDGE,"E176")])]});
            var Q2;
            Q2=makeQuery(id+"F22.opExtrude","SWEPT_EDGE",EDGE,{"disambiguationData":[OSD([sQuery(id+"F21.wireOp",EDGE,"E174"),sQuery(id+"F21.wireOp",EDGE,"E175")])]});
            var Q3;
            Q3=makeQuery(id+"F22.opExtrude","SWEPT_EDGE",EDGE,{"disambiguationData":[OSD([sQuery(id+"F21.wireOp",EDGE,"E175"),sQuery(id+"F21.wireOp",EDGE,"E176")])]});
            var Q4;
            Q4=makeQuery(id+"F22.opExtrude","SWEPT_EDGE",EDGE,{"disambiguationData":[OSD([sQuery(id+"F21.wireOp",EDGE,"E171"),sQuery(id+"F21.wireOp",EDGE,"E172")])]});
            var Q5;
            Q5=makeQuery(id+"F22.opExtrude","SWEPT_EDGE",EDGE,{"disambiguationData":[OSD([sQuery(id+"F21.wireOp",EDGE,"E170"),sQuery(id+"F21.wireOp",EDGE,"E171")])]});
            var Q6;
            Q6=makeQuery(id+"F22.opExtrude","SWEPT_EDGE",EDGE,{"disambiguationData":[OSD([sQuery(id+"F21.wireOp",EDGE,"E169"),sQuery(id+"F21.wireOp",EDGE,"E170")])]});
            var Q7;
            Q7=makeQuery(id+"F22.opExtrude","SWEPT_EDGE",EDGE,{"disambiguationData":[OSD([sQuery(id+"F21.wireOp",EDGE,"E169"),sQuery(id+"F21.wireOp",EDGE,"E172")])]});
            var Q8;
            Q8=makeQuery(id+"F22.opExtrude","SWEPT_EDGE",EDGE,{"disambiguationData":[OSD([sQuery(id+"F21.wireOp",EDGE,"E185"),sQuery(id+"F21.wireOp",EDGE,"E188")])]});
            var Q9;
            Q9=makeQuery(id+"F22.opExtrude","SWEPT_EDGE",EDGE,{"disambiguationData":[OSD([sQuery(id+"F21.wireOp",EDGE,"E185"),sQuery(id+"F21.wireOp",EDGE,"E186")])]});
            var Q10;
            Q10=makeQuery(id+"F22.opExtrude","SWEPT_EDGE",EDGE,{"disambiguationData":[OSD([sQuery(id+"F21.wireOp",EDGE,"E187"),sQuery(id+"F21.wireOp",EDGE,"E188")])]});
            var Q11;
            Q11=makeQuery(id+"F22.opExtrude","SWEPT_EDGE",EDGE,{"disambiguationData":[OSD([sQuery(id+"F21.wireOp",EDGE,"E186"),sQuery(id+"F21.wireOp",EDGE,"E187")])]});
            fillet(context, id + "F23", {"entities" : qUnion([Q0, Q1, Q2, Q3, Q4, Q5, Q6, Q7, Q8, Q9, Q10, Q11]), "radius" : 10 * mm, "tangentPropagation" : true, "allowEdgeOverflow" : false});
        }
        {
            var Q0;
            Q0=makeQuery(id+"F22.opExtrude","SWEPT_BODY",BODY,{"disambiguationData":[OSD([sQuery(id+"F21.wireOp",EDGE,"E173"),sQuery(id+"F21.wireOp",EDGE,"E174"),sQuery(id+"F21.wireOp",EDGE,"E175"),sQuery(id+"F21.wireOp",EDGE,"E176"),sQuery(id+"F21.wireOp",EDGE,"E182"),sQuery(id+"F21.wireOp",EDGE,"E183"),sQuery(id+"F21.wireOp",EDGE,"E184")])]});
            var Q1;
            Q1=makeQuery(id+"F22.opExtrude","SWEPT_BODY",BODY,{"disambiguationData":[OSD([sQuery(id+"F21.wireOp",EDGE,"E169"),sQuery(id+"F21.wireOp",EDGE,"E170"),sQuery(id+"F21.wireOp",EDGE,"E171"),sQuery(id+"F21.wireOp",EDGE,"E172"),sQuery(id+"F21.wireOp",EDGE,"E178"),sQuery(id+"F21.wireOp",EDGE,"E179"),sQuery(id+"F21.wireOp",EDGE,"E180")])]});
            var Q2;
            Q2=makeQuery(id+"F22.opExtrude","SWEPT_BODY",BODY,{"disambiguationData":[OSD([sQuery(id+"F21.wireOp",EDGE,"E185"),sQuery(id+"F21.wireOp",EDGE,"E186"),sQuery(id+"F21.wireOp",EDGE,"E187"),sQuery(id+"F21.wireOp",EDGE,"E188"),sQuery(id+"F21.wireOp",EDGE,"E190"),sQuery(id+"F21.wireOp",EDGE,"E191")])]});
            var Q3;
            Q3=qCreatedBy(id+"F13.planeOp",FACE);
            mirror(context, id + "F24", {"entities" : qUnion([Q0, Q1, Q2]), "mirrorPlane" : qUnion([Q3])});
        }
        {
            var Q0;
            Q0=makeQuery(id+"F16.opExtrude","CAP_FACE",FACE,{"disambiguationData":[OSD([sQuery(id+"F15.wireOp",EDGE,"E116"),sQuery(id+"F15.wireOp",EDGE,"E117"),sQuery(id+"F15.wireOp",EDGE,"E118"),sQuery(id+"F15.wireOp",EDGE,"E119"),sQuery(id+"F15.wireOp",EDGE,"E121"),sQuery(id+"F15.wireOp",EDGE,"E122"),sQuery(id+"F15.wireOp",EDGE,"E123"),sQuery(id+"F15.wireOp",EDGE,"E124"),sQuery(id+"F15.wireOp",EDGE,"E125"),sQuery(id+"F15.wireOp",EDGE,"E126"),sQuery(id+"F15.wireOp",EDGE,"E127"),sQuery(id+"F15.wireOp",EDGE,"E128"),sQuery(id+"F15.wireOp",EDGE,"E129")])],"isStart":true});
            var sketch = newSketch(context, id + "F25", { "sketchPlane" : qUnion([Q0])});
            skLineSegment(sketch, "E192", {"start": v(-300, 821.25) * mm, "end": v(-249, 821.25) * mm});
            skLineSegment(sketch, "E193", {"start": v(-249, 821.25) * mm, "end": v(-249, 920) * mm});
            skLineSegment(sketch, "E194", {"start": v(-249, 920) * mm, "end": v(-300, 920) * mm, "construction": true});
            skLineSegment(sketch, "E195", {"start": v(-300, 920) * mm, "end": v(-300, 821.25) * mm});
            skLineSegment(sketch, "E196", {"start": v(-274.5, 920) * mm, "end": v(-274.5, 821.25) * mm, "construction": true});
            skArc(sketch, "E197", {"start": v(-249, 920) * mm, "mid": v(-274.5, 945.5) * mm, "end": v(-300, 920) * mm});
            skCircle(sketch, "E198", {"center": v(-274.5, 836.25) * mm, "radius": 6.25 * mm});
            skCircle(sketch, "E199", {"center": v(-274.5, 856.25) * mm, "radius": 6.25 * mm});
            skCircle(sketch, "E200", {"center": v(-274.5, 920) * mm, "radius": 6.25 * mm});
            skSolve(sketch);
        }
        {
            var Q0;
            Q0 = qSketchRegion(id + "F25", true);
            extrude(context, id + "F26", {"entities" : qUnion([Q0]), "depth" : 4 * mm, "offsetDistance" : 25 * mm});
        }
        {
            var Q0;
            Q0=makeQuery(id+"F8.opExtrude","CAP_FACE",FACE,{"disambiguationData":[OSD([sQuery(id+"F7.wireOp",EDGE,"E57"),sQuery(id+"F7.wireOp",EDGE,"E58"),sQuery(id+"F7.wireOp",EDGE,"E59"),sQuery(id+"F7.wireOp",EDGE,"E60"),sQuery(id+"F7.wireOp",EDGE,"E63"),sQuery(id+"F7.wireOp",EDGE,"E65"),sQuery(id+"F7.wireOp",EDGE,"E66"),sQuery(id+"F7.wireOp",EDGE,"E67"),sQuery(id+"F7.wireOp",EDGE,"E68"),sQuery(id+"F7.wireOp",EDGE,"E69")])],"isStart":false});
            cPlane(context, id + "F27", {"entities" : qUnion([Q0]), "cplaneType" : CPlaneType.OFFSET, "offset" : 300 * mm, "oppositeDirection" : true, "width" : 150 * mm, "height" : 150 * mm});
        }
        {
            var Q0;
            Q0=makeQuery(id+"F1.opExtrude","SWEPT_BODY",BODY,{"disambiguationData":[OSD([sQuery(id+"F0.wireOp",EDGE,"E0"),sQuery(id+"F0.wireOp",EDGE,"E1"),sQuery(id+"F0.wireOp",EDGE,"E2"),sQuery(id+"F0.wireOp",EDGE,"E3"),sQuery(id+"F0.wireOp",EDGE,"E5"),sQuery(id+"F0.wireOp",EDGE,"E6"),sQuery(id+"F0.wireOp",EDGE,"E7")])]});
            var Q1;
            Q1=makeQuery(id+"F20.opPattern","COPY",BODY,{"derivedFrom":makeQuery(id+"F1.opExtrude","SWEPT_BODY",BODY,{"disambiguationData":[OSD([sQuery(id+"F0.wireOp",EDGE,"E0"),sQuery(id+"F0.wireOp",EDGE,"E1"),sQuery(id+"F0.wireOp",EDGE,"E2"),sQuery(id+"F0.wireOp",EDGE,"E3"),sQuery(id+"F0.wireOp",EDGE,"E5"),sQuery(id+"F0.wireOp",EDGE,"E6"),sQuery(id+"F0.wireOp",EDGE,"E7")])]}),"instanceName":"1"});
            var Q2;
            Q2=makeQuery(id+"F22.opExtrude","SWEPT_BODY",BODY,{"disambiguationData":[OSD([sQuery(id+"F21.wireOp",EDGE,"E173"),sQuery(id+"F21.wireOp",EDGE,"E174"),sQuery(id+"F21.wireOp",EDGE,"E175"),sQuery(id+"F21.wireOp",EDGE,"E176"),sQuery(id+"F21.wireOp",EDGE,"E182"),sQuery(id+"F21.wireOp",EDGE,"E183"),sQuery(id+"F21.wireOp",EDGE,"E184")])]});
            var Q3;
            Q3=makeQuery(id+"F22.opExtrude","SWEPT_BODY",BODY,{"disambiguationData":[OSD([sQuery(id+"F21.wireOp",EDGE,"E169"),sQuery(id+"F21.wireOp",EDGE,"E170"),sQuery(id+"F21.wireOp",EDGE,"E171"),sQuery(id+"F21.wireOp",EDGE,"E172"),sQuery(id+"F21.wireOp",EDGE,"E178"),sQuery(id+"F21.wireOp",EDGE,"E179"),sQuery(id+"F21.wireOp",EDGE,"E180")])]});
            var Q4;
            Q4=makeQuery(id+"F22.opExtrude","SWEPT_BODY",BODY,{"disambiguationData":[OSD([sQuery(id+"F21.wireOp",EDGE,"E185"),sQuery(id+"F21.wireOp",EDGE,"E186"),sQuery(id+"F21.wireOp",EDGE,"E187"),sQuery(id+"F21.wireOp",EDGE,"E188"),sQuery(id+"F21.wireOp",EDGE,"E190"),sQuery(id+"F21.wireOp",EDGE,"E191")])]});
            var Q5;
            Q5=makeQuery(id+"F24.opPattern","COPY",BODY,{"derivedFrom":makeQuery(id+"F22.opExtrude","SWEPT_BODY",BODY,{"disambiguationData":[OSD([sQuery(id+"F21.wireOp",EDGE,"E169"),sQuery(id+"F21.wireOp",EDGE,"E170"),sQuery(id+"F21.wireOp",EDGE,"E171"),sQuery(id+"F21.wireOp",EDGE,"E172"),sQuery(id+"F21.wireOp",EDGE,"E178"),sQuery(id+"F21.wireOp",EDGE,"E179"),sQuery(id+"F21.wireOp",EDGE,"E180")])]}),"instanceName":"1"});
            var Q6;
            Q6=makeQuery(id+"F24.opPattern","COPY",BODY,{"derivedFrom":makeQuery(id+"F22.opExtrude","SWEPT_BODY",BODY,{"disambiguationData":[OSD([sQuery(id+"F21.wireOp",EDGE,"E185"),sQuery(id+"F21.wireOp",EDGE,"E186"),sQuery(id+"F21.wireOp",EDGE,"E187"),sQuery(id+"F21.wireOp",EDGE,"E188"),sQuery(id+"F21.wireOp",EDGE,"E190"),sQuery(id+"F21.wireOp",EDGE,"E191")])]}),"instanceName":"1"});
            var Q7;
            Q7=makeQuery(id+"F24.opPattern","COPY",BODY,{"derivedFrom":makeQuery(id+"F22.opExtrude","SWEPT_BODY",BODY,{"disambiguationData":[OSD([sQuery(id+"F21.wireOp",EDGE,"E173"),sQuery(id+"F21.wireOp",EDGE,"E174"),sQuery(id+"F21.wireOp",EDGE,"E175"),sQuery(id+"F21.wireOp",EDGE,"E176"),sQuery(id+"F21.wireOp",EDGE,"E182"),sQuery(id+"F21.wireOp",EDGE,"E183"),sQuery(id+"F21.wireOp",EDGE,"E184")])]}),"instanceName":"1"});
            var Q8;
            Q8=makeQuery(id+"F8.opExtrude","SWEPT_BODY",BODY,{"disambiguationData":[OSD([sQuery(id+"F7.wireOp",EDGE,"E57"),sQuery(id+"F7.wireOp",EDGE,"E58"),sQuery(id+"F7.wireOp",EDGE,"E59"),sQuery(id+"F7.wireOp",EDGE,"E60"),sQuery(id+"F7.wireOp",EDGE,"E63"),sQuery(id+"F7.wireOp",EDGE,"E65"),sQuery(id+"F7.wireOp",EDGE,"E66"),sQuery(id+"F7.wireOp",EDGE,"E67"),sQuery(id+"F7.wireOp",EDGE,"E68"),sQuery(id+"F7.wireOp",EDGE,"E69")])]});
            var Q9;
            Q9=makeQuery(id+"F16.opExtrude","SWEPT_BODY",BODY,{"disambiguationData":[OSD([sQuery(id+"F15.wireOp",EDGE,"E116"),sQuery(id+"F15.wireOp",EDGE,"E117"),sQuery(id+"F15.wireOp",EDGE,"E118"),sQuery(id+"F15.wireOp",EDGE,"E119"),sQuery(id+"F15.wireOp",EDGE,"E121"),sQuery(id+"F15.wireOp",EDGE,"E122"),sQuery(id+"F15.wireOp",EDGE,"E123"),sQuery(id+"F15.wireOp",EDGE,"E124"),sQuery(id+"F15.wireOp",EDGE,"E125"),sQuery(id+"F15.wireOp",EDGE,"E126"),sQuery(id+"F15.wireOp",EDGE,"E127"),sQuery(id+"F15.wireOp",EDGE,"E128")])]});
            var Q10;
            Q10=makeQuery(id+"F26.opExtrude","SWEPT_BODY",BODY,{"disambiguationData":[OSD([sQuery(id+"F25.wireOp",EDGE,"E192"),sQuery(id+"F25.wireOp",EDGE,"E193"),sQuery(id+"F25.wireOp",EDGE,"E195"),sQuery(id+"F25.wireOp",EDGE,"E197"),sQuery(id+"F25.wireOp",EDGE,"E198"),sQuery(id+"F25.wireOp",EDGE,"E199"),sQuery(id+"F25.wireOp",EDGE,"E200")])]});
            var Q11;
            Q11=qCreatedBy(id+"F27.planeOp",FACE);
            mirror(context, id + "F28", {"entities" : qUnion([Q0, Q1, Q2, Q3, Q4, Q5, Q6, Q7, Q8, Q9, Q10]), "mirrorPlane" : qUnion([Q11])});
        }
        {
            var Q0;
            {var subQ0=sQuery(id+"F0.wireOp",EDGE,"E3");Q0=makeQuery(id+"F6.boolean.opBoolean","SPLIT",FACE,{"disambiguationData":[TD([makeQuery(id+"F6.opExtrude","SWEPT_FACE",FACE,{"disambiguationData":[OSD([sQuery(id+"F5.wireOp",EDGE,"E46.MirrorCS")])]})])],"derivedFrom":makeQuery(id+"F1.opExtrude","SWEPT_FACE",FACE,{"disambiguationData":[OSD([subQ0])]})});}
            var sketch = newSketch(context, id + "F29", { "sketchPlane" : qUnion([Q0])});
            skLineSegment(sketch, "E201", {"start": v(-600, 130) * mm, "end": v(0, 130) * mm});
            skLineSegment(sketch, "E202", {"start": v(0, 130) * mm, "end": v(0, 170) * mm});
            skLineSegment(sketch, "E203", {"start": v(0, 170) * mm, "end": v(-600, 170) * mm});
            skLineSegment(sketch, "E204", {"start": v(-600, 170) * mm, "end": v(-600, 130) * mm});
            skLineSegment(sketch, "E205", {"start": v(-600, 150) * mm, "end": v(0, 150) * mm, "construction": true});
            skCircle(sketch, "E206", {"center": v(-570, 150) * mm, "radius": 6.25 * mm});
            skCircle(sketch, "E207", {"center": v(-30, 150) * mm, "radius": 6.25 * mm});
            skLineSegment(sketch, "E208", {"start": v(0, 320) * mm, "end": v(-600, 320) * mm});
            skLineSegment(sketch, "E209", {"start": v(-600, 320) * mm, "end": v(-600, 280) * mm});
            skLineSegment(sketch, "E210", {"start": v(-600, 280) * mm, "end": v(0, 280) * mm});
            skLineSegment(sketch, "E211", {"start": v(0, 280) * mm, "end": v(0, 320) * mm});
            skLineSegment(sketch, "E212", {"start": v(0, 300) * mm, "end": v(-600, 300) * mm, "construction": true});
            skCircle(sketch, "E213", {"center": v(-570, 300) * mm, "radius": 6.25 * mm});
            skCircle(sketch, "E214", {"center": v(-30, 300) * mm, "radius": 6.25 * mm});
            skSolve(sketch);
        }
        {
            var Q0;
            Q0 = qSketchRegion(id + "F29", true);
            extrude(context, id + "F30", {"entities" : qUnion([Q0]), "depth" : 4 * mm, "offsetDistance" : 25 * mm});
        }
        {
            var Q0;
            Q0=makeQuery(id+"F30.opExtrude","SWEPT_EDGE",EDGE,{"disambiguationData":[OSD([sQuery(id+"F29.wireOp",EDGE,"E203"),sQuery(id+"F29.wireOp",EDGE,"E204")])]});
            var Q1;
            Q1=makeQuery(id+"F30.opExtrude","SWEPT_EDGE",EDGE,{"disambiguationData":[OSD([sQuery(id+"F29.wireOp",EDGE,"E201"),sQuery(id+"F29.wireOp",EDGE,"E204")])]});
            var Q2;
            Q2=makeQuery(id+"F30.opExtrude","SWEPT_EDGE",EDGE,{"disambiguationData":[OSD([sQuery(id+"F29.wireOp",EDGE,"E202"),sQuery(id+"F29.wireOp",EDGE,"E203")])]});
            var Q3;
            Q3=makeQuery(id+"F30.opExtrude","SWEPT_EDGE",EDGE,{"disambiguationData":[OSD([sQuery(id+"F29.wireOp",EDGE,"E201"),sQuery(id+"F29.wireOp",EDGE,"E202")])]});
            var Q4;
            Q4=makeQuery(id+"F30.opExtrude","SWEPT_EDGE",EDGE,{"disambiguationData":[OSD([sQuery(id+"F29.wireOp",EDGE,"E208"),sQuery(id+"F29.wireOp",EDGE,"E209")])]});
            var Q5;
            Q5=makeQuery(id+"F30.opExtrude","SWEPT_EDGE",EDGE,{"disambiguationData":[OSD([sQuery(id+"F29.wireOp",EDGE,"E209"),sQuery(id+"F29.wireOp",EDGE,"E210")])]});
            var Q6;
            Q6=makeQuery(id+"F30.opExtrude","SWEPT_EDGE",EDGE,{"disambiguationData":[OSD([sQuery(id+"F29.wireOp",EDGE,"E210"),sQuery(id+"F29.wireOp",EDGE,"E211")])]});
            var Q7;
            Q7=makeQuery(id+"F30.opExtrude","SWEPT_EDGE",EDGE,{"disambiguationData":[OSD([sQuery(id+"F29.wireOp",EDGE,"E208"),sQuery(id+"F29.wireOp",EDGE,"E211")])]});
            fillet(context, id + "F31", {"entities" : qUnion([Q0, Q1, Q2, Q3, Q4, Q5, Q6, Q7]), "radius" : 10 * mm, "tangentPropagation" : true, "allowEdgeOverflow" : false});
        }
        {
            var Q0;
            Q0=makeQuery(id+"F19.boolean.opBoolean","COPY",FACE,{"derivedFrom":makeQuery(id+"F19.opExtrude","SWEPT_FACE",FACE,{"disambiguationData":[OSD([sQuery(id+"F18.wireOp",EDGE,"E141"),sQuery(id+"F18.wireOp",EDGE,"E159.MirrorCS")])]})});
            var Q1;
            Q1=makeQuery(id+"F19.boolean.opBoolean","COPY",FACE,{"derivedFrom":makeQuery(id+"F19.opExtrude","SWEPT_FACE",FACE,{"disambiguationData":[OSD([sQuery(id+"F18.wireOp",EDGE,"E148.MirrorCS"),sQuery(id+"F18.wireOp",EDGE,"E167.MirrorCS")])]})});
            cPlane(context, id + "F32", {"entities" : qUnion([Q0, Q1]), "cplaneType" : CPlaneType.MID_PLANE, "offset" : 25 * mm, "width" : 150 * mm, "height" : 150 * mm});
        }
        {
            var Q0;
            Q0=makeQuery(id+"F30.opExtrude","SWEPT_BODY",BODY,{"disambiguationData":[OSD([sQuery(id+"F29.wireOp",EDGE,"E201"),sQuery(id+"F29.wireOp",EDGE,"E202"),sQuery(id+"F29.wireOp",EDGE,"E203"),sQuery(id+"F29.wireOp",EDGE,"E204"),sQuery(id+"F29.wireOp",EDGE,"E206"),sQuery(id+"F29.wireOp",EDGE,"E207")])]});
            var Q1;
            Q1=makeQuery(id+"F30.opExtrude","SWEPT_BODY",BODY,{"disambiguationData":[OSD([sQuery(id+"F29.wireOp",EDGE,"E208"),sQuery(id+"F29.wireOp",EDGE,"E209"),sQuery(id+"F29.wireOp",EDGE,"E210"),sQuery(id+"F29.wireOp",EDGE,"E211"),sQuery(id+"F29.wireOp",EDGE,"E213"),sQuery(id+"F29.wireOp",EDGE,"E214")])]});
            var Q2;
            Q2=qCreatedBy(id+"F32.planeOp",FACE);
            mirror(context, id + "F33", {"entities" : qUnion([Q0, Q1]), "mirrorPlane" : qUnion([Q2])});
        }
        {
            var Q0;
            Q0=qCreatedBy(id+"F27.planeOp",FACE);
            var sketch = newSketch(context, id + "F34", { "sketchPlane" : qUnion([Q0])});
            skCircle(sketch, "E215", {"center": v(274.5, 920) * mm, "radius": 5.9 * mm});
            skSolve(sketch);
        }
        {
            var Q0;
            Q0 = qSketchRegion(id + "F34", true);
            extrude(context, id + "F35", {"entities" : qUnion([Q0]), "endBound" : BoundingType.SYMMETRIC, "depth" : 530 * mm, "offsetDistance" : 25 * mm});
        }
        {
            var Q0;
            Q0=qCreatedBy(id+"F27.planeOp",FACE);
            var sketch = newSketch(context, id + "F36", { "sketchPlane" : qUnion([Q0])});
            skCircle(sketch, "E216", {"center": v(274.5, 920) * mm, "radius": 30 * mm});
            skCircle(sketch, "E217", {"center": v(274.5, 920) * mm, "radius": 6.25 * mm});
            skSolve(sketch);
        }
        {
            var Q0;
            Q0 = qSketchRegion(id + "F36", true);
            extrude(context, id + "F37", {"entities" : qUnion([Q0]), "operationType" : NewBodyOperationType.ADD, "endBound" : BoundingType.SYMMETRIC, "depth" : 450 * mm, "offsetDistance" : 25 * mm});
        }
        {
            var Q0;
            Q0=makeQuery(id+"F35.opExtrude","CAP_EDGE",EDGE,{"disambiguationData":[OSD([sQuery(id+"F34.wireOp",EDGE,"E215")])],"isStart":false});
            var Q1;
            Q1=makeQuery(id+"F35.opExtrude","CAP_EDGE",EDGE,{"disambiguationData":[OSD([sQuery(id+"F34.wireOp",EDGE,"E215")])],"isStart":true});
            chamfer(context, id + "F38", {"entities" : qUnion([Q0, Q1]), "width" : 2 * mm, "tangentPropagation" : true});
        }
        {
            var Q0;
            Q0=makeQuery(id+"F37.opExtrude","CAP_EDGE",EDGE,{"disambiguationData":[OSD([sQuery(id+"F36.wireOp",EDGE,"E216")])],"isStart":false});
            var Q1;
            Q1=makeQuery(id+"F37.opExtrude","CAP_EDGE",EDGE,{"disambiguationData":[OSD([sQuery(id+"F36.wireOp",EDGE,"E216")])],"isStart":true});
            chamfer(context, id + "F39", {"entities" : qUnion([Q0, Q1]), "width" : 5 * mm, "tangentPropagation" : true});
        }
        {
            var Q0;
            Q0=makeQuery(id+"F37.opExtrude","SWEPT_FACE",FACE,{"disambiguationData":[OSD([sQuery(id+"F36.wireOp",EDGE,"E216")])]});
            cPlane(context, id + "F40", {"entities" : qUnion([Q0]), "cplaneType" : CPlaneType.LINE_ANGLE, "offset" : 25 * mm, "angle" : 0 * degree, "width" : 150 * mm, "height" : 150 * mm});
        }
    });
